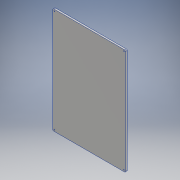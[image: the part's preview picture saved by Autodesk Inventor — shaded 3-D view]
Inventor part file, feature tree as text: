
AUTODESK INVENTOR PART (.ipt)
format: ipt  version: 2017.3 (Build 213256000, 256)  size: 122,368 bytes
history: native  units: mm
features: sketch x2, sheet_metal_op x1, fillet x1, hole x1, other x1
ambient origin geometry x8: Origin, YZ Plane, XZ Plane, XY Plane, X Axis, Y Axis, Z Axis, Center Point
bodies: Solid1 (feature_tree)
feature tree (6):
  sheet_metal_op  "Face1"
  fillet  "Fillet1"  Radius=220.0mm
  hole  "Hole1"  [1 undecoded]
  sketch  "Sketch1"  dims[d1=320.0mm d2=5.0mm]
  other  "Plate1"
  sketch  "Sketch2"  dims[d3=3.0mm d4=310.0mm d5=210.0mm d6=3.2mm d9=3.0mm d10=6.0mm d11=5.0mm d12=2.0mm d13=90.0deg d14=8.8mm d15=0.0mm]
note: 1 required parameter value undecoded (feature->parameter linkage not recoverable at this tier; creation-order binding heuristic only, values carry confidence <= 0.55)
